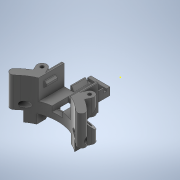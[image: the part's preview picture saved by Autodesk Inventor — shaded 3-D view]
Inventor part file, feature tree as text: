
AUTODESK INVENTOR PART (.ipt)
format: ipt  version: 2020 (Build 240168000, 168)  size: 985,600 bytes
history: native  units: mm
features: projected_geometry x35, extrude x22, sketch x22, other x6, chamfer x3, sweep x1, fillet x1
ambient origin geometry x8: Origin, YZ Plane, XZ Plane, XY Plane, X Axis, Y Axis, Z Axis, Center Point
bodies: Body1 (feature_tree)
feature tree (90):
  other  "Твердое тело1"
  extrude  "Выдавливание1"  Depth=35.0mm TaperAngle=0.0deg
  sketch  "Эскиз2"
  extrude  "Выдавливание2"  Depth=4.0mm
  sweep  "Сдвиг1"
  extrude  "Выдавливание5"  Depth=8.0mm
  extrude  "Выдавливание6"  Depth=35.0mm TaperAngle=0.0deg
  extrude  "Выдавливание7"  Depth=8.5mm
  extrude  "Выдавливание8"  TaperAngle=45.0deg  [1 undecoded]
  other  "РабПлоскость1"
  extrude  "Выдавливание9"  Depth=8.5mm
  extrude  "Выдавливание10"  TaperAngle=45.0deg  [1 undecoded]
  extrude  "Выдавливание11"  TaperAngle=0.0deg  [1 undecoded]
  sketch  "Эскиз13"
  other  "РабПлоскость2"
  sketch  "Эскиз14"
  extrude  "Выдавливание12"  Depth=5.0mm TaperAngle=0.0deg
  extrude  "Выдавливание13"  Depth=15.0mm TaperAngle=0.0deg
  other  "РабПлоскость3"
  extrude  "Выдавливание14"  Depth=15.0mm TaperAngle=0.0deg
  extrude  "Выдавливание15"  Depth=26.0mm
  extrude  "Выдавливание16"  Depth=6.0mm
  extrude  "Выдавливание17"  Depth=15.0mm TaperAngle=0.0deg
  chamfer  "Фаска1"  Distance=2.0mm
  other  "РабПлоскость4"
  sketch  "Эскиз18"
  extrude  "Выдавливание18"  Depth=1.5mm
  extrude  "Выдавливание19"  Depth=3.0mm
  extrude  "Выдавливание20"  Depth=6.0mm
  chamfer  "Фаска2"  Distance=2.5mm
  fillet  "Сопряжение1"  [1 undecoded]
  extrude  "Выдавливание21"  Depth=15.0mm TaperAngle=0.0deg
  extrude  "Выдавливание22"  Depth=7.0mm TaperAngle=0.0deg
  extrude  "Выдавливание23"  Depth=7.0mm TaperAngle=0.0deg
  other  "РабПлоскость5"
  extrude  "Выдавливание24"  Depth=40.0mm
  chamfer  "Фаска3"  Distance=2.9mm
  sketch  "Эскиз24"
  sketch  "Эскиз1"
  sketch  "Эскиз3"
  projected_geometry  "Спроецированная петля1"
  projected_geometry  "Спроецированная петля2"
  sketch  "3D эскиз1"
  sketch  "Эскиз4"
  sketch  "Эскиз6"
  projected_geometry  "Спроецированная петля4"
  sketch  "Эскиз7"
  projected_geometry  "Спроецированная петля5"
  sketch  "Эскиз9"
  projected_geometry  "Спроецированная петля7"
  sketch  "Эскиз11"
  projected_geometry  "Спроецированная петля8"
  sketch  "Эскиз12"
  projected_geometry  "Спроецированная петля9"
  projected_geometry  "Спроецированная петля10"
  sketch  "Эскиз15"
  sketch  "Эскиз16"
  projected_geometry  "Спроецированная петля11"
  projected_geometry  "Спроецированная петля12"
  sketch  "Эскиз17"
  projected_geometry  "Спроецированная петля13"
  projected_geometry  "Спроецированная петля14"
  projected_geometry  "Спроецированная петля15"
  projected_geometry  "Спроецированная петля16"
  sketch  "Эскиз19"
  projected_geometry  "Спроецированная петля17"
  sketch  "Эскиз20"
  projected_geometry  "Спроецированная петля18"
  projected_geometry  "Спроецированная петля19"
  projected_geometry  "Спроецированная петля20"
  projected_geometry  "Спроецированная петля21"
  projected_geometry  "Спроецированная петля22"
  projected_geometry  "Спроецированная петля23"
  sketch  "Эскиз21"
  projected_geometry  "Спроецированная петля24"
  projected_geometry  "Спроецированная петля25"
  projected_geometry  "Спроецированная петля26"
  projected_geometry  "Спроецированная петля27"
  projected_geometry  "Спроецированная петля28"
  projected_geometry  "Спроецированная петля29"
  projected_geometry  "Спроецированная петля30"
  projected_geometry  "Спроецированная петля31"
  sketch  "Эскиз22"
  projected_geometry  "Спроецированная петля32"
  projected_geometry  "Спроецированная петля33"
  sketch  "Эскиз23"
  projected_geometry  "Спроецированная петля34"
  projected_geometry  "Спроецированная петля35"
  projected_geometry  "Спроецированная петля36"
  projected_geometry  "Спроецированная петля37"
note: 4 required parameter values undecoded (feature->parameter linkage not recoverable at this tier; creation-order binding heuristic only, values carry confidence <= 0.55)
